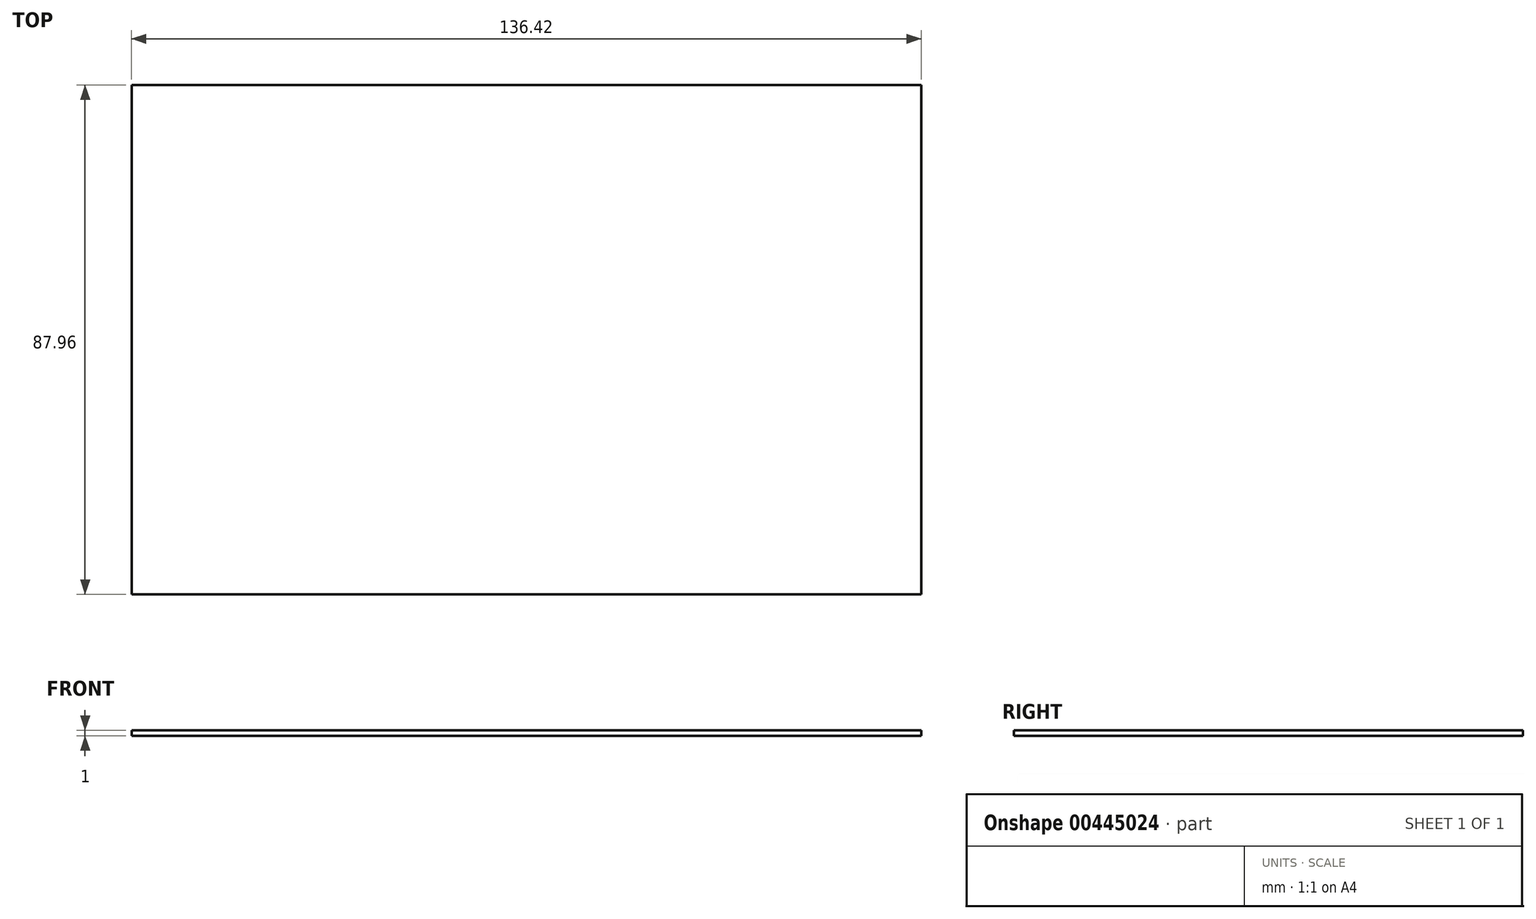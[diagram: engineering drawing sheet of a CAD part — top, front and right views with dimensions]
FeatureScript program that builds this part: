
annotation { "Feature Type Name" : "Feature", "Feature Type Description" : "" }
export const myFeature = defineFeature(function(context is Context, id is Id, definition is map)
    precondition{}
    {
        {
            var Q0;
            Q0=qCreatedBy(makeId("Top.planeOp"),FACE);
            var sketch = newSketch(context, id + "F0", { "sketchPlane" : qUnion([Q0])});
            skLineSegment(sketch, "E0.bottom", {"start": v(-68.2, 43.98) * mm, "end": v(68.2, 43.98) * mm});
            skLineSegment(sketch, "E0.top", {"start": v(-68.2, -43.98) * mm, "end": v(68.2, -43.98) * mm});
            skLineSegment(sketch, "E0.left", {"start": v(-68.2, 43.98) * mm, "end": v(-68.2, -43.98) * mm});
            skLineSegment(sketch, "E0.right", {"start": v(68.2, 43.98) * mm, "end": v(68.2, -43.98) * mm});
            skPoint(sketch, "E0.middle", {"position": v(0, 0) * mm});
            skSolve(sketch);
        }
        {
            var Q0;
            Q0=makeQuery(id+"F0.imprint","IMPRINT",FACE,{"disambiguationData":[TD([[makeQuery(id+"F0.imprint","IMPRINT",EDGE,{"derivedFrom":sQuery(id+"F0.wireOp",EDGE,"E0.bottom")}),-1.0]])]});
            extrude(context, id + "F1", {"entities" : qUnion([Q0]), "depth" : 1 * mm});
        }
    });
